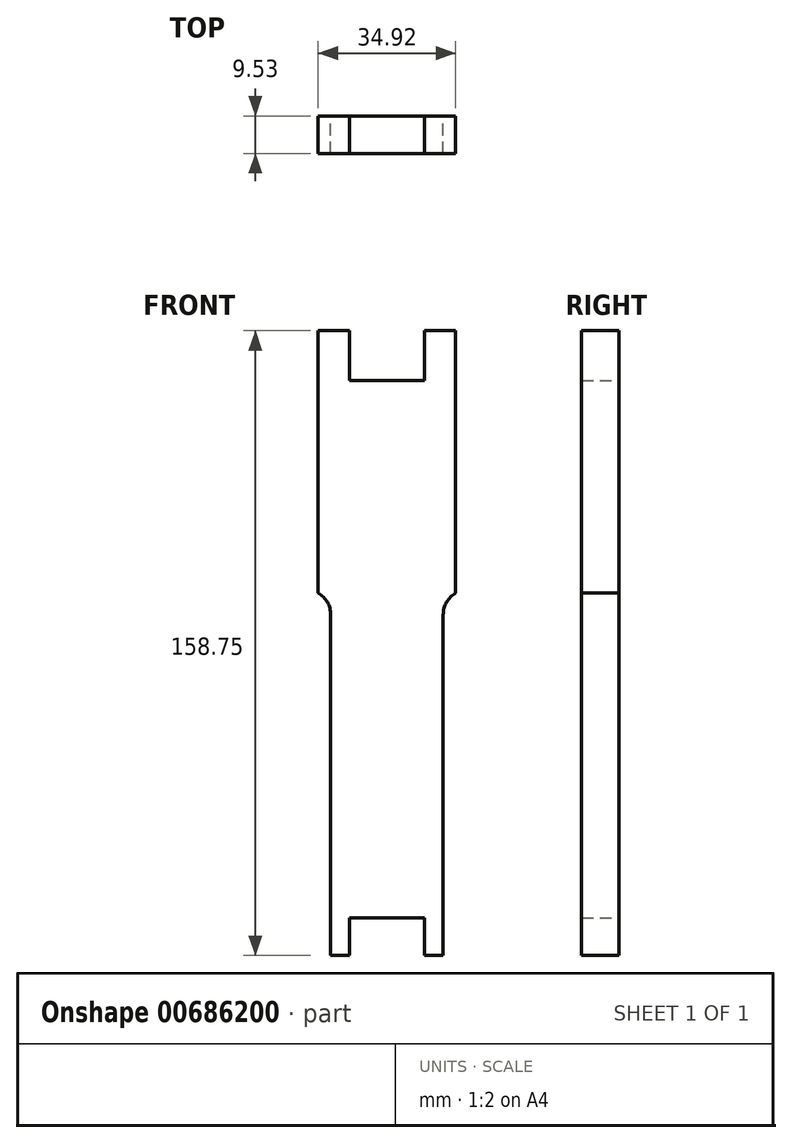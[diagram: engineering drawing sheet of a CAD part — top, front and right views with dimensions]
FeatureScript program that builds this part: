
annotation { "Feature Type Name" : "Feature", "Feature Type Description" : "" }
export const myFeature = defineFeature(function(context is Context, id is Id, definition is map)
    precondition{}
    {
        {
            var Q0;
            Q0=qCreatedBy(makeId("Front.planeOp"),FACE);
            var sketch = newSketch(context, id + "F0", { "sketchPlane" : qUnion([Q0])});
            skLineSegment(sketch, "E0", {"start": v(-9.53, 158.75) * mm, "end": v(-17.46, 158.75) * mm});
            skLineSegment(sketch, "E1", {"start": v(-17.46, 158.75) * mm, "end": v(-17.46, 92.07) * mm});
            skArc(sketch, "E2", {"start": v(-17.46, 92.07) * mm, "mid": v(-15.14, 89.75) * mm, "end": v(-14.29, 86.58) * mm});
            skLineSegment(sketch, "E3", {"start": v(-14.29, 86.58) * mm, "end": v(-14.29, 0) * mm});
            skLineSegment(sketch, "E4", {"start": v(-14.29, 0) * mm, "end": v(-9.52, 0) * mm});
            skLineSegment(sketch, "E5", {"start": v(0, 9.53) * mm, "end": v(0, 146.05) * mm});
            skLineSegment(sketch, "E6", {"start": v(0, 54.28) * mm, "end": v(0, 9.53) * mm, "construction": true});
            skLineSegment(sketch, "E7", {"start": v(-9.53, 158.75) * mm, "end": v(-9.53, 146.05) * mm});
            skLineSegment(sketch, "E8", {"start": v(-9.53, 146.05) * mm, "end": v(0, 146.05) * mm});
            skPoint(sketch, "E9.orphan", {"position": v(0, 158.75) * mm});
            skLineSegment(sketch, "E10", {"start": v(-9.52, 0) * mm, "end": v(-9.52, 9.53) * mm});
            skLineSegment(sketch, "E11", {"start": v(-9.52, 9.53) * mm, "end": v(0, 9.53) * mm});
            skLineSegment(sketch, "E12.trimOffspring", {"start": v(0, 0) * mm, "end": v(0, -56.36) * mm, "construction": true});
            skSolve(sketch);
        }
        {
            var Q0;
            Q0 = qSketchRegion(id + "F0", true);
            extrude(context, id + "F1", {"entities" : qUnion([Q0]), "depth" : 9.52 * mm, "offsetDistance" : 25.4 * mm});
        }
        {
            var Q0;
            Q0=makeQuery(id+"F1.opExtrude","SWEPT_BODY",BODY,{"disambiguationData":[OSD([sQuery(id+"F0.wireOp",EDGE,"E0"),sQuery(id+"F0.wireOp",EDGE,"E1"),sQuery(id+"F0.wireOp",EDGE,"d87df990-b306-4542-905a-bac74690506b"),sQuery(id+"F0.wireOp",EDGE,"E2"),sQuery(id+"F0.wireOp",EDGE,"E3"),sQuery(id+"F0.wireOp",EDGE,"E4"),sQuery(id+"F0.wireOp",EDGE,"E5")])]});
            var Q1;
            Q1=qCreatedBy(makeId("Right.planeOp"),FACE);
            mirror(context, id + "F2", {"operationType" : NewBodyOperationType.ADD, "entities" : qUnion([Q0]), "mirrorPlane" : qUnion([Q1])});
        }
    });
